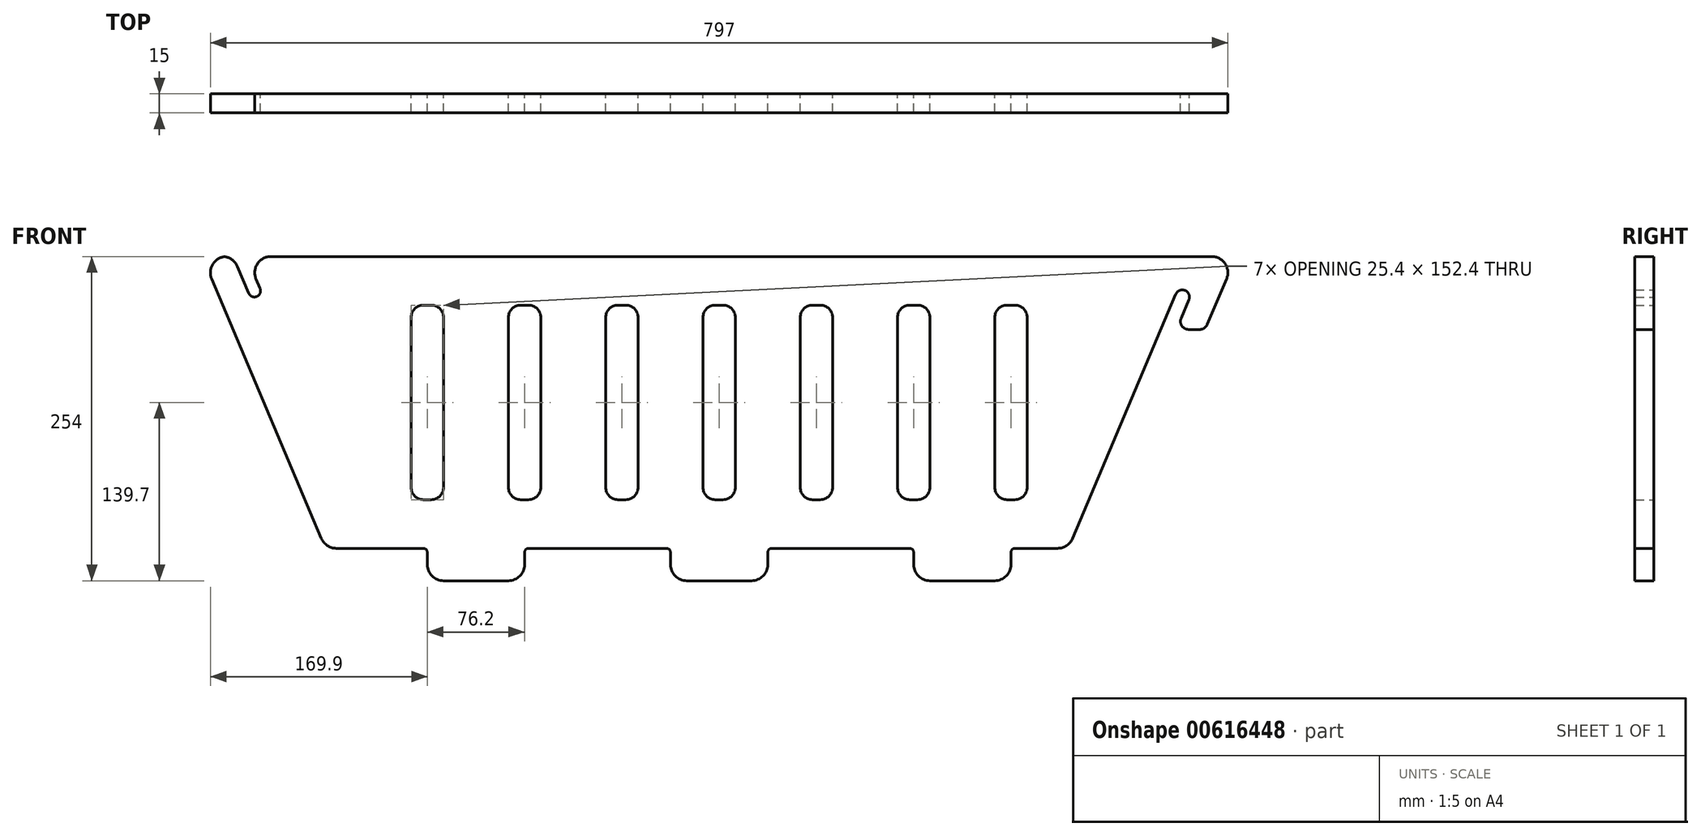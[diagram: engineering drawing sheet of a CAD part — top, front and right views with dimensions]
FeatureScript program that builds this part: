
annotation { "Feature Type Name" : "Feature", "Feature Type Description" : "" }
export const myFeature = defineFeature(function(context is Context, id is Id, definition is map)
    precondition{}
    {
        {
            var Q0;
            Q0=qCreatedBy(makeId("Front.planeOp"),FACE);
            var sketch = newSketch(context, id + "F0", { "sketchPlane" : qUnion([Q0])});
            skArc(sketch, "E0", {"start": v(152.4, -114.3) * mm, "mid": v(156.12, -123.28) * mm, "end": v(165.1, -127) * mm});
            skLineSegment(sketch, "E1", {"start": v(152.4, -114.3) * mm, "end": v(152.4, -104.77) * mm});
            skArc(sketch, "E2", {"start": v(152.4, -104.77) * mm, "mid": v(151.47, -102.53) * mm, "end": v(149.23, -101.6) * mm});
            skLineSegment(sketch, "E3", {"start": v(149.23, -101.6) * mm, "end": v(41.28, -101.6) * mm});
            skArc(sketch, "E4", {"start": v(41.28, -101.6) * mm, "mid": v(39.03, -102.53) * mm, "end": v(38.1, -104.77) * mm});
            skLineSegment(sketch, "E5", {"start": v(38.1, -114.3) * mm, "end": v(38.1, -104.77) * mm});
            skArc(sketch, "E6", {"start": v(25.4, -127) * mm, "mid": v(34.38, -123.28) * mm, "end": v(38.1, -114.3) * mm});
            skLineSegment(sketch, "E7", {"start": v(25.4, -127) * mm, "end": v(-25.4, -127) * mm});
            skArc(sketch, "E8", {"start": v(-38.1, -114.3) * mm, "mid": v(-34.38, -123.28) * mm, "end": v(-25.4, -127) * mm});
            skLineSegment(sketch, "E9", {"start": v(-38.1, -114.3) * mm, "end": v(-38.1, -104.77) * mm});
            skArc(sketch, "E10", {"start": v(-38.1, -104.77) * mm, "mid": v(-39.03, -102.53) * mm, "end": v(-41.28, -101.6) * mm});
            skLineSegment(sketch, "E11", {"start": v(-41.28, -101.6) * mm, "end": v(-149.23, -101.6) * mm});
            skLineSegment(sketch, "E12", {"start": v(-152.4, -114.3) * mm, "end": v(-152.4, -104.77) * mm});
            skArc(sketch, "E13", {"start": v(-165.1, -127) * mm, "mid": v(-156.12, -123.28) * mm, "end": v(-152.4, -114.3) * mm});
            skLineSegment(sketch, "E14", {"start": v(-165.1, -127) * mm, "end": v(-215.9, -127) * mm});
            skLineSegment(sketch, "E15", {"start": v(-228.6, -114.3) * mm, "end": v(-228.6, -104.77) * mm});
            skArc(sketch, "E16", {"start": v(-228.6, -104.77) * mm, "mid": v(-229.53, -102.53) * mm, "end": v(-231.78, -101.6) * mm});
            skLineSegment(sketch, "E17", {"start": v(-231.78, -101.6) * mm, "end": v(-299.92, -101.6) * mm});
            skArc(sketch, "E18", {"start": v(-311.62, -93.84) * mm, "mid": v(-306.94, -99.48) * mm, "end": v(-299.92, -101.6) * mm});
            skLineSegment(sketch, "E19", {"start": v(-397.5, 109.36) * mm, "end": v(-311.62, -93.84) * mm});
            skArc(sketch, "E20", {"start": v(-389.1, 126.56) * mm, "mid": v(-397.22, 119.87) * mm, "end": v(-397.5, 109.36) * mm});
            skArc(sketch, "E21", {"start": v(-385.8, 126.56) * mm, "mid": v(-387.45, 126.78) * mm, "end": v(-389.1, 126.56) * mm});
            skArc(sketch, "E22", {"start": v(-377.41, 119.24) * mm, "mid": v(-380.76, 123.87) * mm, "end": v(-385.8, 126.56) * mm});
            skLineSegment(sketch, "E23", {"start": v(-377.41, 119.24) * mm, "end": v(-368.52, 98.2) * mm});
            skArc(sketch, "E24", {"start": v(-368.52, 98.2) * mm, "mid": v(-362.2, 95.63) * mm, "end": v(-359.63, 101.95) * mm});
            skLineSegment(sketch, "E25", {"start": v(-359.63, 101.95) * mm, "end": v(-362.75, 109.36) * mm});
            skArc(sketch, "E26", {"start": v(-351.06, 127) * mm, "mid": v(-361.64, 121.32) * mm, "end": v(-362.75, 109.36) * mm});
            skLineSegment(sketch, "E27", {"start": v(385.8, 127) * mm, "end": v(-351.06, 127) * mm});
            skArc(sketch, "E28", {"start": v(397.5, 109.36) * mm, "mid": v(396.39, 121.32) * mm, "end": v(385.8, 127) * mm});
            skLineSegment(sketch, "E29", {"start": v(397.5, 109.36) * mm, "end": v(382.44, 73.73) * mm});
            skArc(sketch, "E30", {"start": v(376.6, 69.85) * mm, "mid": v(380.1, 70.9) * mm, "end": v(382.44, 73.73) * mm});
            skLineSegment(sketch, "E31", {"start": v(376.6, 69.85) * mm, "end": v(367.77, 69.85) * mm});
            skArc(sketch, "E32", {"start": v(361.92, 78.67) * mm, "mid": v(362.48, 72.7) * mm, "end": v(367.77, 69.85) * mm});
            skLineSegment(sketch, "E33", {"start": v(361.92, 78.67) * mm, "end": v(368, 93.07) * mm});
            skArc(sketch, "E34", {"start": v(368, 93.07) * mm, "mid": v(365.03, 100.4) * mm, "end": v(357.71, 97.43) * mm});
            skLineSegment(sketch, "E35", {"start": v(357.71, 97.43) * mm, "end": v(276.88, -93.84) * mm});
            skArc(sketch, "E36", {"start": v(265.18, -101.6) * mm, "mid": v(272.2, -99.48) * mm, "end": v(276.88, -93.84) * mm});
            skLineSegment(sketch, "E37", {"start": v(265.18, -101.6) * mm, "end": v(231.78, -101.6) * mm});
            skArc(sketch, "E38", {"start": v(231.78, -101.6) * mm, "mid": v(229.53, -102.53) * mm, "end": v(228.6, -104.77) * mm});
            skLineSegment(sketch, "E39", {"start": v(228.6, -114.3) * mm, "end": v(228.6, -104.77) * mm});
            skArc(sketch, "E40", {"start": v(215.9, -127) * mm, "mid": v(224.88, -123.28) * mm, "end": v(228.6, -114.3) * mm});
            skLineSegment(sketch, "E41", {"start": v(215.9, -127) * mm, "end": v(165.1, -127) * mm});
            skArc(sketch, "E42", {"start": v(3.05, -63.5) * mm, "mid": v(9.87, -60.67) * mm, "end": v(12.7, -53.85) * mm});
            skLineSegment(sketch, "E43", {"start": v(12.7, -53.85) * mm, "end": v(12.7, 79.25) * mm});
            skArc(sketch, "E44", {"start": v(12.7, 79.25) * mm, "mid": v(9.87, 86.07) * mm, "end": v(3.05, 88.9) * mm});
            skLineSegment(sketch, "E45", {"start": v(3.05, 88.9) * mm, "end": v(-3.05, 88.9) * mm});
            skArc(sketch, "E46", {"start": v(-3.05, 88.9) * mm, "mid": v(-9.87, 86.07) * mm, "end": v(-12.7, 79.25) * mm});
            skLineSegment(sketch, "E47", {"start": v(-12.7, 79.25) * mm, "end": v(-12.7, -53.85) * mm});
            skArc(sketch, "E48", {"start": v(-12.7, -53.85) * mm, "mid": v(-9.87, -60.67) * mm, "end": v(-3.05, -63.5) * mm});
            skLineSegment(sketch, "E49", {"start": v(-3.05, -63.5) * mm, "end": v(3.05, -63.5) * mm});
            skArc(sketch, "E50", {"start": v(79.25, -63.5) * mm, "mid": v(86.07, -60.67) * mm, "end": v(88.9, -53.85) * mm});
            skLineSegment(sketch, "E51", {"start": v(88.9, -53.85) * mm, "end": v(88.9, 79.25) * mm});
            skArc(sketch, "E52", {"start": v(88.9, 79.25) * mm, "mid": v(86.07, 86.07) * mm, "end": v(79.25, 88.9) * mm});
            skLineSegment(sketch, "E53", {"start": v(79.25, 88.9) * mm, "end": v(73.15, 88.9) * mm});
            skArc(sketch, "E54", {"start": v(73.15, 88.9) * mm, "mid": v(66.33, 86.07) * mm, "end": v(63.5, 79.25) * mm});
            skLineSegment(sketch, "E55", {"start": v(63.5, 79.25) * mm, "end": v(63.5, -53.85) * mm});
            skArc(sketch, "E56", {"start": v(63.5, -53.85) * mm, "mid": v(66.33, -60.67) * mm, "end": v(73.15, -63.5) * mm});
            skLineSegment(sketch, "E57", {"start": v(73.15, -63.5) * mm, "end": v(79.25, -63.5) * mm});
            skArc(sketch, "E58", {"start": v(155.45, -63.5) * mm, "mid": v(162.27, -60.67) * mm, "end": v(165.1, -53.85) * mm});
            skLineSegment(sketch, "E59", {"start": v(165.1, -53.85) * mm, "end": v(165.1, 79.25) * mm});
            skArc(sketch, "E60", {"start": v(165.1, 79.25) * mm, "mid": v(162.27, 86.07) * mm, "end": v(155.45, 88.9) * mm});
            skLineSegment(sketch, "E61", {"start": v(155.45, 88.9) * mm, "end": v(149.35, 88.9) * mm});
            skArc(sketch, "E62", {"start": v(149.35, 88.9) * mm, "mid": v(142.53, 86.07) * mm, "end": v(139.7, 79.25) * mm});
            skLineSegment(sketch, "E63", {"start": v(139.7, 79.25) * mm, "end": v(139.7, -53.85) * mm});
            skArc(sketch, "E64", {"start": v(139.7, -53.85) * mm, "mid": v(142.53, -60.67) * mm, "end": v(149.35, -63.5) * mm});
            skLineSegment(sketch, "E65", {"start": v(149.35, -63.5) * mm, "end": v(155.45, -63.5) * mm});
            skArc(sketch, "E66", {"start": v(231.65, -63.5) * mm, "mid": v(238.47, -60.67) * mm, "end": v(241.3, -53.85) * mm});
            skLineSegment(sketch, "E67", {"start": v(241.3, -53.85) * mm, "end": v(241.3, 79.25) * mm});
            skArc(sketch, "E68", {"start": v(241.3, 79.25) * mm, "mid": v(238.47, 86.07) * mm, "end": v(231.65, 88.9) * mm});
            skLineSegment(sketch, "E69", {"start": v(231.65, 88.9) * mm, "end": v(225.55, 88.9) * mm});
            skArc(sketch, "E70", {"start": v(225.55, 88.9) * mm, "mid": v(218.73, 86.07) * mm, "end": v(215.9, 79.25) * mm});
            skLineSegment(sketch, "E71", {"start": v(215.9, 79.25) * mm, "end": v(215.9, -53.85) * mm});
            skArc(sketch, "E72", {"start": v(215.9, -53.85) * mm, "mid": v(218.73, -60.67) * mm, "end": v(225.55, -63.5) * mm});
            skLineSegment(sketch, "E73", {"start": v(225.55, -63.5) * mm, "end": v(231.65, -63.5) * mm});
            skArc(sketch, "E74", {"start": v(-73.15, -63.5) * mm, "mid": v(-66.33, -60.67) * mm, "end": v(-63.5, -53.85) * mm});
            skLineSegment(sketch, "E75", {"start": v(-63.5, -53.85) * mm, "end": v(-63.5, 79.25) * mm});
            skArc(sketch, "E76", {"start": v(-63.5, 79.25) * mm, "mid": v(-66.33, 86.07) * mm, "end": v(-73.15, 88.9) * mm});
            skLineSegment(sketch, "E77", {"start": v(-73.15, 88.9) * mm, "end": v(-79.25, 88.9) * mm});
            skArc(sketch, "E78", {"start": v(-79.25, 88.9) * mm, "mid": v(-86.07, 86.07) * mm, "end": v(-88.9, 79.25) * mm});
            skLineSegment(sketch, "E79", {"start": v(-88.9, 79.25) * mm, "end": v(-88.9, -53.85) * mm});
            skArc(sketch, "E80", {"start": v(-88.9, -53.85) * mm, "mid": v(-86.07, -60.67) * mm, "end": v(-79.25, -63.5) * mm});
            skLineSegment(sketch, "E81", {"start": v(-79.25, -63.5) * mm, "end": v(-73.15, -63.5) * mm});
            skArc(sketch, "E82", {"start": v(-149.35, -63.5) * mm, "mid": v(-142.53, -60.67) * mm, "end": v(-139.7, -53.85) * mm});
            skLineSegment(sketch, "E83", {"start": v(-139.7, -53.85) * mm, "end": v(-139.7, 79.25) * mm});
            skArc(sketch, "E84", {"start": v(-139.7, 79.25) * mm, "mid": v(-142.53, 86.07) * mm, "end": v(-149.35, 88.9) * mm});
            skLineSegment(sketch, "E85", {"start": v(-149.35, 88.9) * mm, "end": v(-155.45, 88.9) * mm});
            skArc(sketch, "E86", {"start": v(-155.45, 88.9) * mm, "mid": v(-162.27, 86.07) * mm, "end": v(-165.1, 79.25) * mm});
            skLineSegment(sketch, "E87", {"start": v(-165.1, 79.25) * mm, "end": v(-165.1, -53.85) * mm});
            skArc(sketch, "E88", {"start": v(-165.1, -53.85) * mm, "mid": v(-162.27, -60.67) * mm, "end": v(-155.45, -63.5) * mm});
            skLineSegment(sketch, "E89", {"start": v(-155.45, -63.5) * mm, "end": v(-149.35, -63.5) * mm});
            skArc(sketch, "E90", {"start": v(-225.55, -63.5) * mm, "mid": v(-218.73, -60.67) * mm, "end": v(-215.9, -53.85) * mm});
            skLineSegment(sketch, "E91", {"start": v(-215.9, -53.85) * mm, "end": v(-215.9, 79.25) * mm});
            skArc(sketch, "E92", {"start": v(-215.9, 79.25) * mm, "mid": v(-218.73, 86.07) * mm, "end": v(-225.55, 88.9) * mm});
            skLineSegment(sketch, "E93", {"start": v(-225.55, 88.9) * mm, "end": v(-231.65, 88.9) * mm});
            skArc(sketch, "E94", {"start": v(-231.65, 88.9) * mm, "mid": v(-238.47, 86.07) * mm, "end": v(-241.3, 79.25) * mm});
            skLineSegment(sketch, "E95", {"start": v(-241.3, 79.25) * mm, "end": v(-241.3, -53.85) * mm});
            skArc(sketch, "E96", {"start": v(-241.3, -53.85) * mm, "mid": v(-238.47, -60.67) * mm, "end": v(-231.65, -63.5) * mm});
            skLineSegment(sketch, "E97", {"start": v(-231.65, -63.5) * mm, "end": v(-225.55, -63.5) * mm});
            skArc(sketch, "E98", {"start": v(-149.23, -101.6) * mm, "mid": v(-151.47, -102.53) * mm, "end": v(-152.4, -104.77) * mm});
            skArc(sketch, "E99", {"start": v(-228.6, -114.3) * mm, "mid": v(-224.88, -123.28) * mm, "end": v(-215.9, -127) * mm});
            skSolve(sketch);
        }
        {
            var Q0;
            Q0=makeQuery(id+"F0.imprint","IMPRINT",FACE,{"disambiguationData":[TD([[makeQuery(id+"F0.imprint","IMPRINT",EDGE,{"derivedFrom":sQuery(id+"F0.wireOp",EDGE,"E0")}),1.0]])]});
            extrude(context, id + "F1", {"entities" : qUnion([Q0]), "depth" : 15 * mm, "offsetDistance" : 25 * mm});
        }
    });
